# Revit family: Talos RDR-E01
name_source: partatom
category: Türen
revit_build: Autodesk Revit 2016 (Build: 20150220_1215(x64)
units: mm (PartAtom-declared; Revit-internal decimal feet)

## family parameters
Beim Laden mit Abzugskörper schneiden = Nein
Gemeinsam genutzt = Nein
Immer vertikal = Ja
OmniClass-Nummer = 23.30.10.00
OmniClass-Titel = Doors
Raumberechnungspunkt = Nein

## types (10) — shared parameters
Analytische Konstruktion = <Keine Auswahl>
ClearWidth = 2100 mm
CoverMaterial = <Nach Kategorie>
Design country = Germany
Dicke = 63 mm  [stored 0.206693 ft]
Edition number = 1
ElementWeight = 0.00 kg
FrameMaterial = <Nach Kategorie>
Funktion = Außen
HandlePosition = 35 mm  [stored 0.114829 ft]
HasCover = Ja
HasGrabHandles = Ja
Manufacturer = Kaba GmbH
Manufacturer country = Germany
Manufacturer name = DORMA
Material main = Glass
Material secondary = Metal
Modell = Talos RDR-E01
Nominal height = 2300
OperatingWeight = 0.00 kg
Product Guid = 5c75d33a-c963-4db4-a6cf-dde6d4fceb71
Product SKU = Talos_RDR-E01
RubberMaterial = Zellkautschuk - EPDM
SectionWidth = 4300 mm
Technical description = http://www.kaba.com
Type = Talos RDR-E01
URL = http://www.kaba.com
Weight = 0.00 kg
zero-valued in all types: Nominal width

## per-type parameters (varying)
- RDR-E01 2000: AccessLengthOrRadius=1030 mm; AccessWidth=2000 mm; BaseType=>= 60mm; ClearHeight=2100 mm; CoverWidth=200 mm  [stored 0.656168 ft]; Diameter=1060 mm  [stored 3.47769 ft]; DiameterCoverFront=1140 mm  [stored 3.74016 ft]; DiameterGlassInside=1040 mm  [stored 3.41207 ft]; DiameterGlassOutside=1050 mm  [stored 3.44488 ft]; DiameterNightLock=1090 mm  [stored 3.57612 ft]; DiameterNightLockCover=1120 mm; DiameterNightLockGlassInside=1101 mm; DiameterNightLockGlassOutside=1109 mm  [stored 3.63845 ft]; DoorWidth=970 mm; HandleMaterial=PA6.6 Gf30(schwarz); HasBuiltInAlarm=Nein; HasGrabHandles 120=Nein; HasGrabHandles 180=Ja; HasIntegralShutOffDevice=Nein; HasLock=Nein; HasLockInside=Nein; Height=2300 mm; Hersteller=Kaba GmbH; Konstruktionstyp=Rovolving Door; MotorDriveType=-; NominalWidthOrDiameter=2100 mm; OuterDiameter=2100 mm; Radar=1060 mm  [stored 3.47769 ft]; RotationInterval 120=Nein; RotationInterval 180=Ja; ShutOffDevice=Nein; ShutOffDeviceInside=Nein; StandardUsed=1; Width=2100 mm
- RDR-E01 2200: AccessLengthOrRadius=1130 mm; AccessWidth=2200 mm; BaseType=>= 280 mm; ClearHeight=2300 mm; CoverWidth=200 mm  [stored 0.656168 ft]; Diameter=1160 mm; DiameterCoverFront=1240 mm; DiameterGlassInside=1140 mm  [stored 3.74016 ft]; DiameterGlassOutside=1150 mm  [stored 3.77297 ft]; DiameterNightLock=1190 mm  [stored 3.9042 ft]; DiameterNightLockCover=1220 mm  [stored 4.00262 ft]; DiameterNightLockGlassInside=1201 mm; DiameterNightLockGlassOutside=1209 mm  [stored 3.96654 ft]; DoorWidth=1070 mm; HandleMaterial=1.4401 - A4; HasBuiltInAlarm=Ja; HasGrabHandles 120=Ja; HasGrabHandles 180=Nein; HasIntegralShutOffDevice=Nein; HasLock=Nein; HasLockInside=Nein; Height=2500 mm; Hersteller=Kaba GmbH; Konstruktionstyp=Revolving Door; MotorDriveType=K8-SA1/G4-SA3; NominalWidthOrDiameter=2300 mm; OuterDiameter=2300 mm; Radar=1160 mm; RotationInterval 120=Ja; RotationInterval 180=Nein; ShutOffDevice=Nein; ShutOffDeviceInside=Nein; StandardUsed=2; Width=2300 mm
- RDR-E01 2400: AccessLengthOrRadius=1230 mm  [stored 4.03543 ft]; AccessWidth=2400 mm; BaseType=>= 280 mm; ClearHeight=2300 mm; CoverWidth=200 mm  [stored 0.656168 ft]; Diameter=1260 mm  [stored 4.13386 ft]; DiameterCoverFront=1340 mm  [stored 4.39633 ft]; DiameterGlassInside=1240 mm; DiameterGlassOutside=1250 mm  [stored 4.10105 ft]; DiameterNightLock=1290 mm  [stored 4.23228 ft]; DiameterNightLockCover=1320 mm  [stored 4.33071 ft]; DiameterNightLockGlassInside=1301 mm; DiameterNightLockGlassOutside=1309 mm  [stored 4.29462 ft]; DoorWidth=1170 mm  [stored 3.83858 ft]; HandleMaterial=PA6.6 Gf30(schwarz); HasBuiltInAlarm=Nein; HasGrabHandles 120=Nein; HasGrabHandles 180=Ja; HasIntegralShutOffDevice=Nein; HasLock=Nein; HasLockInside=Nein; Height=2500 mm; Hersteller=Kaba GmbH; Konstruktionstyp=Revolving Door; MotorDriveType=K8-SA2; NominalWidthOrDiameter=2500 mm; OuterDiameter=2500; Radar=1260 mm  [stored 4.13386 ft]; RotationInterval 120=Nein; RotationInterval 180=Ja; ShutOffDevice=Nein; ShutOffDeviceInside=Nein; StandardUsed=3; Width=2500 mm
- RDR-E01 2600: AccessLengthOrRadius=1330 mm  [stored 4.36352 ft]; AccessWidth=2600 mm; BaseType=>= 280 mm; ClearHeight=2300 mm; CoverWidth=100 mm  [stored 0.328084 ft]; Diameter=1360 mm  [stored 4.46194 ft]; DiameterCoverFront=1440 mm; DiameterGlassInside=1340 mm  [stored 4.39633 ft]; DiameterGlassOutside=1350 mm  [stored 4.42913 ft]; DiameterNightLock=1390 mm  [stored 4.56037 ft]; DiameterNightLockCover=1420 mm; DiameterNightLockGlassInside=1401 mm  [stored 4.59646 ft]; DiameterNightLockGlassOutside=1409 mm; DoorWidth=1270 mm; HandleMaterial=1.4401 - A4; HasBuiltInAlarm=Nein; HasGrabHandles 120=Ja; HasGrabHandles 180=Nein; HasIntegralShutOffDevice=Nein; HasLock=Ja; HasLockInside=Nein; Height=2400 mm; Hersteller=Kaba GmbH; Konstruktionstyp=Revolving Door; MotorDriveType=K8-SA1/G4-SA3; NominalWidthOrDiameter=2700 mm; OuterDiameter=2700; Radar=1360 mm  [stored 4.46194 ft]; RotationInterval 120=Ja; RotationInterval 180=Nein; ShutOffDevice=Nein; ShutOffDeviceInside=Nein; StandardUsed=4; Width=2700 mm
- RDR-E01 2800: AccessLengthOrRadius=1430 mm; AccessWidth=2800 mm; BaseType=>= 280 mm; ClearHeight=2100 mm; CoverWidth=300 mm; Diameter=1460 mm; DiameterCoverFront=1540 mm; DiameterGlassInside=1440 mm; DiameterGlassOutside=1450 mm; DiameterNightLock=1490 mm; DiameterNightLockCover=1520 mm; DiameterNightLockGlassInside=1501 mm; DiameterNightLockGlassOutside=1509 mm; DoorWidth=1370 mm; HandleMaterial=PA6.6 Gf30(schwarz); HasBuiltInAlarm=Nein; HasGrabHandles 120=Nein; HasGrabHandles 180=Ja; HasIntegralShutOffDevice=Ja; HasLock=Ja; HasLockInside=Nein; Height=2400 mm; Hersteller=Kaba GmbH; Konstruktionstyp=Revolving Door; MotorDriveType=K8-SA1/G4-SA3; NominalWidthOrDiameter=2900 mm; OuterDiameter=2900; Radar=1460 mm; RotationInterval 120=Nein; RotationInterval 180=Ja; ShutOffDevice=Nein; ShutOffDeviceInside=Ja; StandardUsed=5; Width=2900 mm
- RDR-E01 3000: AccessLengthOrRadius=1530 mm; AccessWidth=3000 mm; BaseType=>= 280 mm; ClearHeight=2300 mm; CoverWidth=300 mm; Diameter=1560 mm; DiameterCoverFront=1640 mm; DiameterGlassInside=1540 mm; DiameterGlassOutside=1550 mm; DiameterNightLock=1590 mm; DiameterNightLockCover=1620 mm; DiameterNightLockGlassInside=1601 mm; DiameterNightLockGlassOutside=1609 mm; DoorWidth=1470 mm; HandleMaterial=1.4401 - A4; HasBuiltInAlarm=Nein; HasGrabHandles 120=Ja; HasGrabHandles 180=Nein; HasIntegralShutOffDevice=Ja; HasLock=Ja; HasLockInside=Nein; Height=2600 mm; Hersteller=Kaba GmbH; Konstruktionstyp=Revolving Door; MotorDriveType=K8-SA1; NominalWidthOrDiameter=3100 mm; OuterDiameter=3100; Radar=1560 mm; RotationInterval 120=Ja; RotationInterval 180=Nein; ShutOffDevice=Nein; ShutOffDeviceInside=Ja; StandardUsed=6; Width=3100 mm
- RDR-E01 3200: AccessLengthOrRadius=1630 mm; AccessWidth=3200 mm; BaseType=>= 60 mm; ClearHeight=2300 mm; CoverWidth=300 mm; Diameter=1660 mm; DiameterCoverFront=1740 mm; DiameterGlassInside=1640 mm; DiameterGlassOutside=1650 mm; DiameterNightLock=1690 mm; DiameterNightLockCover=1720 mm; DiameterNightLockGlassInside=1701 mm; DiameterNightLockGlassOutside=1709 mm; DoorWidth=1570 mm; HandleMaterial=PA6.6 Gf30(schwarz); HasBuiltInAlarm=Nein; HasGrabHandles 120=Nein; HasGrabHandles 180=Ja; HasIntegralShutOffDevice=Ja; HasLock=Nein; HasLockInside=Ja; Height=2600 mm; Hersteller=Kaba GmbH; Konstruktionstyp=Revolving Door; MotorDriveType=-; NominalWidthOrDiameter=3300 mm; OuterDiameter=3300; Radar=1740 mm; RotationInterval 120=Nein; RotationInterval 180=Ja; ShutOffDevice=Ja; ShutOffDeviceInside=Nein; StandardUsed=7; Width=3300 mm
- RDR-E01 3400: AccessLengthOrRadius=1730 mm; AccessWidth=3400 mm; BaseType=>= 60 mm; ClearHeight=2300 mm; CoverWidth=100 mm  [stored 0.328084 ft]; Diameter=1760 mm; DiameterCoverFront=1840 mm; DiameterGlassInside=1740 mm; DiameterGlassOutside=1750 mm; DiameterNightLock=1790 mm; DiameterNightLockCover=1820 mm; DiameterNightLockGlassInside=1801 mm; DiameterNightLockGlassOutside=1809 mm; DoorWidth=1670 mm; HandleMaterial=1.4401 - A4; HasBuiltInAlarm=Nein; HasGrabHandles 120=Ja; HasGrabHandles 180=Nein; HasIntegralShutOffDevice=Nein; HasLock=Nein; HasLockInside=Ja; Height=2400 mm; Hersteller=Kaba GmbH; Konstruktionstyp=Revolving Door; MotorDriveType=-; NominalWidthOrDiameter=3500 mm; OuterDiameter=3500; Radar=1840 mm; RotationInterval 120=Ja; RotationInterval 180=Nein; ShutOffDevice=Nein; ShutOffDeviceInside=Nein; StandardUsed=8; Width=3500 mm
- RDR-E01 3600: AccessLengthOrRadius=1830 mm; AccessWidth=3600 mm; BaseType=>= 280 mm; ClearHeight=2200 mm; CoverWidth=100 mm  [stored 0.328084 ft]; Diameter=1860 mm; DiameterCoverFront=1940 mm; DiameterGlassInside=1840 mm; DiameterGlassOutside=1850 mm; DiameterNightLock=1890 mm; DiameterNightLockCover=1920 mm; DiameterNightLockGlassInside=1901 mm; DiameterNightLockGlassOutside=1909 mm; DoorWidth=1770 mm; HandleMaterial=PA6.6 Gf30(schwarz); HasBuiltInAlarm=Nein; HasGrabHandles 120=Nein; HasGrabHandles 180=Ja; HasIntegralShutOffDevice=Nein; HasLock=Nein; HasLockInside=Nein; Height=2300 mm; Hersteller=Kaba GmbH; Konstruktionstyp=Revolving Door; MotorDriveType=K8-SA1/G4-SA3; NominalWidthOrDiameter=3700 mm; OuterDiameter=3700; Radar=1860 mm; RotationInterval 120=Nein; RotationInterval 180=Ja; ShutOffDevice=Nein; ShutOffDeviceInside=Nein; StandardUsed=9; Width=3700 mm
- RDR-E01 3700: AccessLengthOrRadius=1880 mm; AccessWidth=3700 mm; BaseType=>= 280 mm; ClearHeight=2300 mm; CoverWidth=300 mm; Diameter=1910 mm; DiameterCoverFront=1990 mm; DiameterGlassInside=1890 mm; DiameterGlassOutside=1900 mm; DiameterNightLock=1940 mm; DiameterNightLockCover=1970 mm; DiameterNightLockGlassInside=1951 mm; DiameterNightLockGlassOutside=1959 mm; DoorWidth=1820 mm; HandleMaterial=1.4401 - A4; HasBuiltInAlarm=Ja; HasGrabHandles 120=Nein; HasGrabHandles 180=Ja; HasIntegralShutOffDevice=Nein; HasLock=Nein; HasLockInside=Nein; Height=2600 mm; Hersteller=kaba GmbH; Konstruktionstyp=Revolving Door; MotorDriveType=K8-SA1/G4-SA3; NominalWidthOrDiameter=3800 mm; OuterDiameter=3800; Radar=1910 mm; RotationInterval 120=Nein; RotationInterval 180=Ja; ShutOffDevice=Nein; ShutOffDeviceInside=Nein; StandardUsed=10; Width=3800 mm

note: [stored X ft] marks values corroborated as IEEE doubles in the binary element streams (Revit-internal decimal feet)
